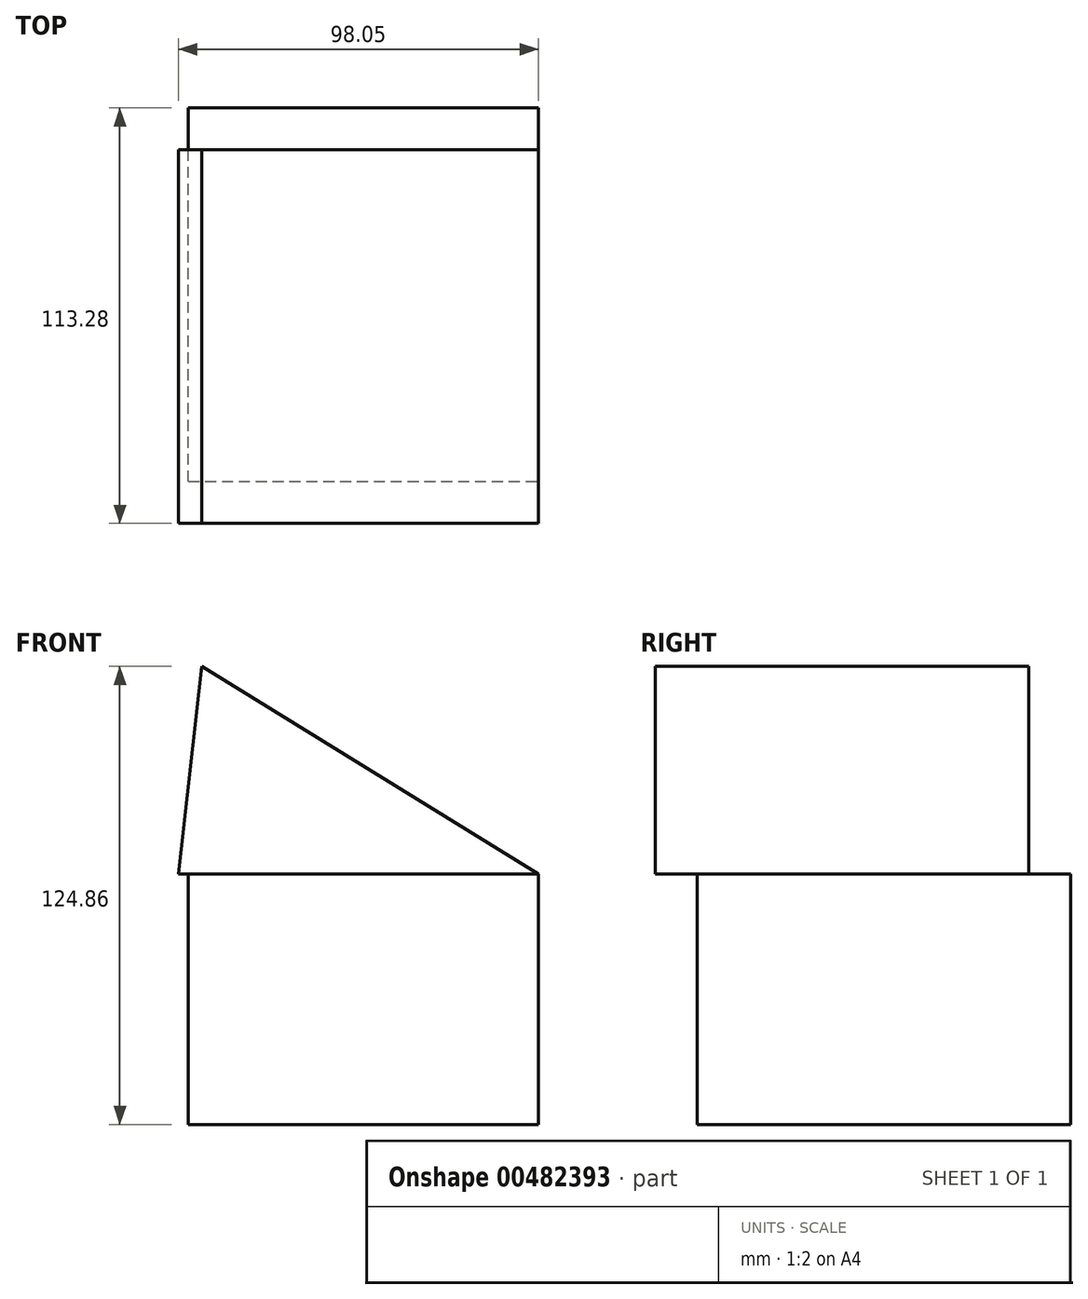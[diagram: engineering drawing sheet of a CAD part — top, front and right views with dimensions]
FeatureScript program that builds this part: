
annotation { "Feature Type Name" : "Feature", "Feature Type Description" : "" }
export const myFeature = defineFeature(function(context is Context, id is Id, definition is map)
    precondition{}
    {
        {
            var Q0;
            Q0=qCreatedBy(makeId("Front.planeOp"),FACE);
            var sketch = newSketch(context, id + "F0", { "sketchPlane" : qUnion([Q0])});
            skLineSegment(sketch, "E0.bottom", {"start": v(-3.91, 0) * mm, "end": v(91.5, 0) * mm});
            skLineSegment(sketch, "E0.top", {"start": v(-3.91, -68.27) * mm, "end": v(91.5, -68.27) * mm});
            skLineSegment(sketch, "E0.left", {"start": v(-3.91, 0) * mm, "end": v(-3.91, -68.27) * mm});
            skLineSegment(sketch, "E0.right", {"start": v(91.5, 0) * mm, "end": v(91.5, -68.27) * mm});
            skSolve(sketch);
        }
        {
            var Q0;
            Q0 = qSketchRegion(id + "F0", true);
            extrude(context, id + "F1", {"entities" : qUnion([Q0]), "depth" : 101.85 * mm});
        }
        {
            var Q0;
            Q0=makeQuery(id+"F1.opExtrude","CAP_FACE",FACE,{"disambiguationData":[OSD([sQuery(id+"F0.wireOp",EDGE,"E0.bottom"),sQuery(id+"F0.wireOp",EDGE,"E0.top"),sQuery(id+"F0.wireOp",EDGE,"E0.left"),sQuery(id+"F0.wireOp",EDGE,"E0.right")])],"isStart":false});
            var sketch = newSketch(context, id + "F2", { "sketchPlane" : qUnion([Q0])});
            skLineSegment(sketch, "E1", {"start": v(-6.54, 0) * mm, "end": v(0, 59.21) * mm});
            skLineSegment(sketch, "E2", {"start": v(-0.29, 56.59) * mm, "end": v(91.5, 0) * mm});
            skLineSegment(sketch, "E3", {"start": v(91.5, 0) * mm, "end": v(-6.54, 0) * mm});
            skSolve(sketch);
        }
        {
            var Q0;
            Q0 = qSketchRegion(id + "F2", true);
            extrude(context, id + "F3", {"entities" : qUnion([Q0]), "operationType" : NewBodyOperationType.ADD, "oppositeDirection" : true, "depth" : 90.42 * mm, "hasSecondDirection" : true, "secondDirectionOppositeDirection" : false, "secondDirectionDepth" : 11.43 * mm});
        }
    });
